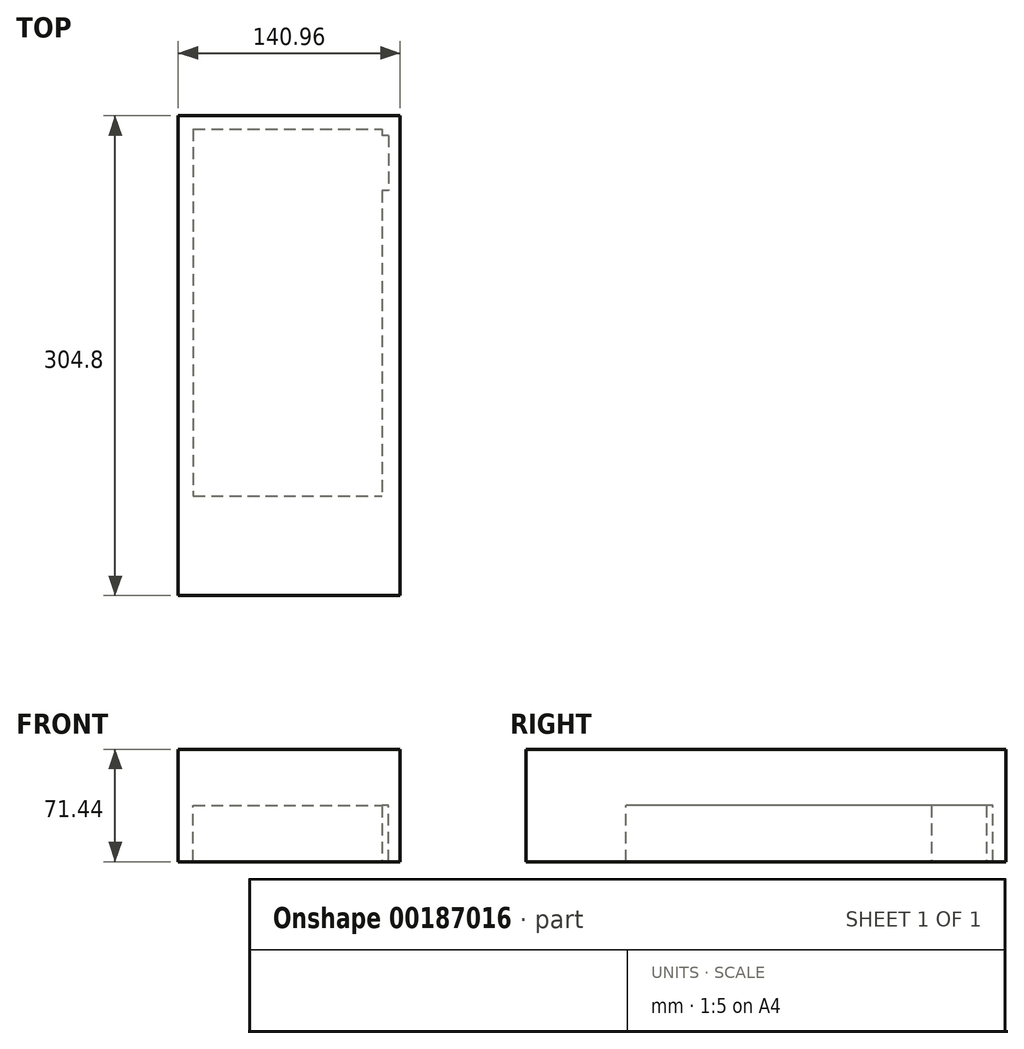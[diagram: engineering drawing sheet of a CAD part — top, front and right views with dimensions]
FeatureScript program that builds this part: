
annotation { "Feature Type Name" : "Feature", "Feature Type Description" : "" }
export const myFeature = defineFeature(function(context is Context, id is Id, definition is map)
    precondition{}
    {
        {
            var Q0;
            Q0=qCreatedBy(makeId("Front.planeOp"),FACE);
            var sketch = newSketch(context, id + "F0", { "sketchPlane" : qUnion([Q0])});
            skLineSegment(sketch, "E0.bottom", {"start": v(-70.48, 35.72) * mm, "end": v(70.48, 35.72) * mm});
            skLineSegment(sketch, "E0.top", {"start": v(-70.48, -35.72) * mm, "end": v(70.48, -35.72) * mm});
            skLineSegment(sketch, "E0.left", {"start": v(-70.48, 35.72) * mm, "end": v(-70.48, -35.72) * mm});
            skLineSegment(sketch, "E0.right", {"start": v(70.48, 35.72) * mm, "end": v(70.48, -35.72) * mm});
            skPoint(sketch, "E0.middle", {"position": v(0, 0) * mm});
            skSolve(sketch);
        }
        {
            var Q0;
            Q0 = qSketchRegion(id + "F0", true);
            extrude(context, id + "F1", {"entities" : qUnion([Q0]), "depth" : 304.8 * mm});
        }
        {
            var Q0;
            Q0=qCreatedBy(makeId("Top.planeOp"),FACE);
            var sketch = newSketch(context, id + "F2", { "sketchPlane" : qUnion([Q0])});
            skLineSegment(sketch, "E1.bottom", {"start": v(-60.9, -8.4) * mm, "end": v(58.97, -8.4) * mm});
            skLineSegment(sketch, "E1.top", {"start": v(-60.9, -241.4) * mm, "end": v(58.97, -241.4) * mm});
            skLineSegment(sketch, "E1.left", {"start": v(-60.9, -8.4) * mm, "end": v(-60.9, -241.4) * mm});
            skLineSegment(sketch, "E1.right", {"start": v(58.97, -8.4) * mm, "end": v(58.97, -241.4) * mm});
            skSolve(sketch);
        }
        {
            var Q0;
            Q0 = qSketchRegion(id + "F2", true);
            extrude(context, id + "F3", {"entities" : qUnion([Q0]), "operationType" : NewBodyOperationType.REMOVE, "oppositeDirection" : true, "depth" : 152.4 * mm});
        }
        {
            var Q0;
            Q0=qCreatedBy(makeId("Top.planeOp"),FACE);
            var sketch = newSketch(context, id + "F4", { "sketchPlane" : qUnion([Q0])});
            skLineSegment(sketch, "E2.bottom", {"start": v(63.05, -12.47) * mm, "end": v(27.09, -12.47) * mm});
            skLineSegment(sketch, "E2.top", {"start": v(63.05, -47.47) * mm, "end": v(27.09, -47.47) * mm});
            skLineSegment(sketch, "E2.left", {"start": v(63.05, -12.47) * mm, "end": v(63.05, -47.47) * mm});
            skLineSegment(sketch, "E2.right", {"start": v(27.09, -12.47) * mm, "end": v(27.09, -47.47) * mm});
            skSolve(sketch);
        }
        {
            var Q0;
            Q0 = qSketchRegion(id + "F4", true);
            extrude(context, id + "F5", {"entities" : qUnion([Q0]), "operationType" : NewBodyOperationType.REMOVE, "oppositeDirection" : true, "depth" : 254 * mm});
        }
        {
            var Q0;
            Q0=qCreatedBy(makeId("Front.planeOp"),FACE);
            var sketch = newSketch(context, id + "F6", { "sketchPlane" : qUnion([Q0])});
            skCircle(sketch, "E3", {"center": v(-40.51, 16.78) * mm, "radius": 11.87 * mm});
            skSolve(sketch);
        }
        {
            var Q0;
            Q0=makeQuery(id+"F6.imprint","IMPRINT",FACE,{"disambiguationData":[TD([[makeQuery(id+"F6.imprint","IMPRINT",EDGE,{"derivedFrom":sQuery(id+"F6.wireOp",EDGE,"E3")}),1.0]])]});
            extrude(context, id + "F7", {"entities" : qUnion([Q0]), "operationType" : NewBodyOperationType.REMOVE, "oppositeDirection" : true, "depth" : 304.8 * mm});
        }
    });
